# Revit family: Electronics_Expanders_Biamp_Tesira_4-Channel-Input-and-Output_EX-IO__
name_source: partatom
category: Communication Devices
units: mm (PartAtom-declared; Revit-internal decimal feet)

## family parameters
Cut with Voids When Loaded = No
Host = Face
Maintain Annotation Orientation = No
OmniClass Number = 23.85.10.11.11
OmniClass Title = Sound and Signal Devices
Part Type = Normal
Room Calculation Point = No
Round Connector Dimension = Use Diameter
Shared = No

## types (1)
- EX-IO
    A/D - D/A Converters = 24-bit
    Apparent Load = 0 VA
    Compliance = FCC Part 15B (USA); CE marked (Europe); UL and C-UL listed (USA & Canada); RCM (Australia); EAC (Eurasian Customs Union); RoHS Directive (Europe)
    Connector Description = PoE+ (IEEE 802.3at Class 4, 30W)
    Cross Talk = 0dB Gain, +4dBu In: < -85dB channel to channel at 1kHz; 54dB Gain, -50dBu In: < -75dB channel to channel at 1kHz;
    Default Elevation = 4' - 0"
    Depth = 0' - 7 3/4"
    Description = Tesira® EX-IO 4-Channel Input and Output Expanders
    Dynamic Range = > 108dB at 20Hz~20kHz, 0dB
    EIN = < -125dBu at 20Hz~20kHz, 66dB Gain, 150 ohm
    Frequency Response = +0/-0.25dB 20Hz~20kHz at +4dBu
    Height = 0' - 1 3/4"
    Housing Material = Biamp - Metal - Silver
    Input Gain Range = 0 - 66dB at 6dB Steps
    Input Impedance = 8 kohm (balanced)
    Manufacturer = Biamp
    Max Power Consumption = 0 W
    Maximum Input = +24dBu
    Maximum Output = +24dBu
    Model = Tesira EX-IO
    No mount = No mount
    Number of Poles = 1
    Output Impedance = 200 ohm
    Phantom Power = +48 VDC (7mA/input)
    Power Factor = 1
    Product Documentation Link = https://downloads.biamp.com
    Product Page URL = https://www.biamp.com
    Product data url = https://www.bimobject.com
    RMK-1 = RMK-1
    RMK-2 = RMK-2
    Sampling Rate = 48kHz
    THD+N = 0dB Gain, +4dBu In: < 0.006% at 20Hz~20kHz; 54dB Gain, -50dBu In: < 0.040% at 20Hz~20kHz;
    URL = https://www.biamp.com
    UTMK-1 = UTMK-1
    Voltage = 0 V
    Weight = 3.00 lbf
    Width = 0' - 8 1/2"

## geometry (parser evidence)
native form markers: Sweep x13
no freeform markers — native parametric forms only
